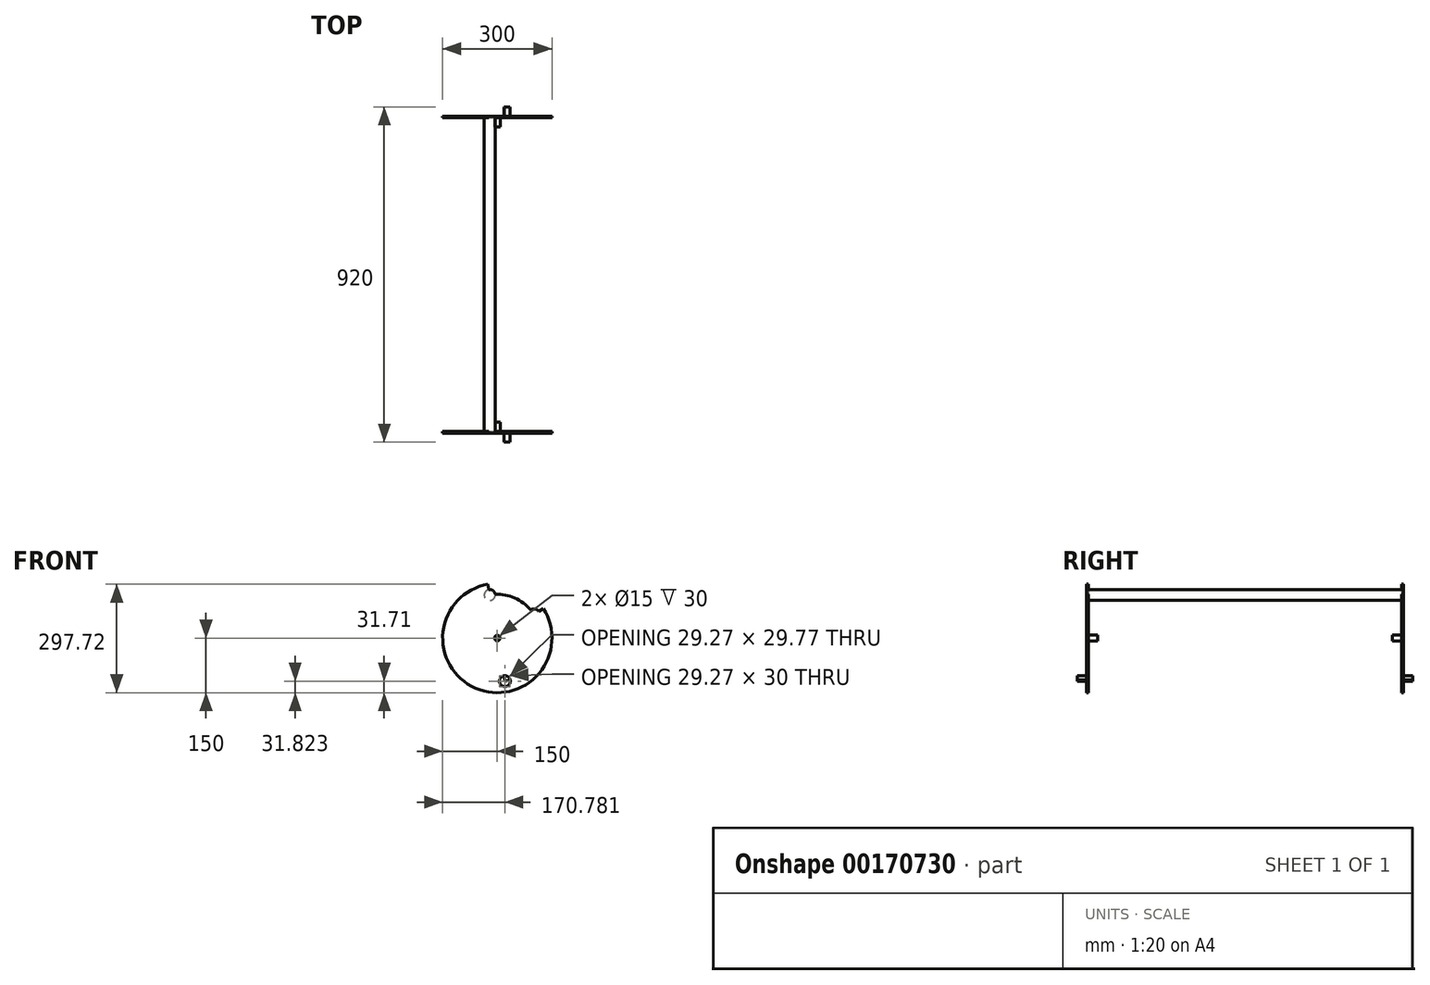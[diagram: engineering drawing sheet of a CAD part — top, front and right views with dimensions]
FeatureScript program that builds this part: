
annotation { "Feature Type Name" : "Feature", "Feature Type Description" : "" }
export const myFeature = defineFeature(function(context is Context, id is Id, definition is map)
    precondition{}
    {
        {
            var Q0;
            Q0=qCreatedBy(makeId("Front.planeOp"),FACE);
            var sketch = newSketch(context, id + "F0", { "sketchPlane" : qUnion([Q0])});
            skCircle(sketch, "E0", {"center": v(0, 0) * mm, "radius": 150 * mm});
            skLineSegment(sketch, "E1", {"start": v(0, 0) * mm, "end": v(459.5, 297.1) * mm});
            skLineSegment(sketch, "E2", {"start": v(0, 0) * mm, "end": v(728.16, 0) * mm});
            skLineSegment(sketch, "E3", {"start": v(0, 0) * mm, "end": v(0, -535.69) * mm});
            skLineSegment(sketch, "E4", {"start": v(125.96, 81.44) * mm, "end": v(100.77, 65.16) * mm});
            skCircle(sketch, "E5", {"center": v(100.77, 65.16) * mm, "radius": 15 * mm});
            skCircle(sketch, "E6", {"center": v(0, 0) * mm, "radius": 8.5 * mm});
            skCircle(sketch, "E7", {"center": v(0, 0) * mm, "radius": 7.5 * mm});
            skLineSegment(sketch, "E8", {"start": v(100.77, 65.16) * mm, "end": v(20.84, -118.18) * mm});
            skLineSegment(sketch, "E9", {"start": v(0, 0) * mm, "end": v(20.84, -118.18) * mm});
            skLineSegment(sketch, "E10", {"start": v(0, 0) * mm, "end": v(34.47, -195.47) * mm});
            skLineSegment(sketch, "E11", {"start": v(34.47, -195.47) * mm, "end": v(-30.52, 173.11) * mm});
            skCircle(sketch, "E12", {"center": v(20.84, -118.18) * mm, "radius": 15 * mm});
            skCircle(sketch, "E13", {"center": v(0, 0) * mm, "radius": 120 * mm});
            skCircle(sketch, "E14", {"center": v(-20.84, 118.18) * mm, "radius": 15 * mm});
            skSolve(sketch);
        }
        {
            var Q0;
            {var subQ0=sQuery(id+"F0.wireOp",EDGE,"E7");var subQ1=sQuery(id+"F0.wireOp",EDGE,"E2");var subQ2=makeQuery(id+"F0.imprint","INTERSECT",VERTEX,{"derivedFrom":[subQ1,subQ0]});Q0=makeQuery(id+"F0.imprint","IMPRINT",FACE,{"disambiguationData":[TD([[makeQuery(id+"F0.imprint","IMPRINT",EDGE,{"disambiguationData":[TD([[subQ2,-1.0]])],"derivedFrom":subQ1}),-1.0]])]});}
            var Q1;
            {var subQ0=sQuery(id+"F0.wireOp",EDGE,"E7");var subQ1=sQuery(id+"F0.wireOp",EDGE,"E1");var subQ2=makeQuery(id+"F0.imprint","INTERSECT",VERTEX,{"derivedFrom":[subQ1,subQ0]});Q1=makeQuery(id+"F0.imprint","IMPRINT",FACE,{"disambiguationData":[TD([[makeQuery(id+"F0.imprint","IMPRINT",EDGE,{"disambiguationData":[TD([[subQ2,-1.0]])],"derivedFrom":subQ1}),-1.0]])]});}
            var Q2;
            {var subQ0=sQuery(id+"F0.wireOp",EDGE,"E7");var subQ1=sQuery(id+"F0.wireOp",EDGE,"E3");var subQ2=makeQuery(id+"F0.imprint","INTERSECT",VERTEX,{"derivedFrom":[subQ1,subQ0]});Q2=makeQuery(id+"F0.imprint","IMPRINT",FACE,{"disambiguationData":[TD([[makeQuery(id+"F0.imprint","IMPRINT",EDGE,{"disambiguationData":[TD([[subQ2,-1.0]])],"derivedFrom":subQ1}),-1.0]])]});}
            var Q3;
            {var subQ0=sQuery(id+"F0.wireOp",EDGE,"E7");var subQ1=sQuery(id+"F0.wireOp",EDGE,"E3");var subQ2=makeQuery(id+"F0.imprint","INTERSECT",VERTEX,{"derivedFrom":[subQ1,subQ0]});Q3=makeQuery(id+"F0.imprint","IMPRINT",FACE,{"disambiguationData":[TD([[makeQuery(id+"F0.imprint","IMPRINT",EDGE,{"disambiguationData":[TD([[subQ2,-1.0]])],"derivedFrom":subQ1}),1.0]])]});}
            var Q4;
            {var subQ0=sQuery(id+"F0.wireOp",EDGE,"E7");var subQ1=sQuery(id+"F0.wireOp",EDGE,"E1");var subQ2=makeQuery(id+"F0.imprint","INTERSECT",VERTEX,{"derivedFrom":[subQ1,subQ0]});Q4=makeQuery(id+"F0.imprint","IMPRINT",FACE,{"disambiguationData":[TD([[makeQuery(id+"F0.imprint","IMPRINT",EDGE,{"disambiguationData":[TD([[subQ2,-1.0]])],"derivedFrom":subQ1}),1.0]])]});}
            extrude(context, id + "F1", {"entities" : qUnion([Q0, Q1, Q2, Q3, Q4]), "oppositeDirection" : true, "depth" : 25 * mm});
        }
        {
            var Q0;
            {var subQ0=sQuery(id+"F0.wireOp",EDGE,"E13");var subQ1=sQuery(id+"F0.wireOp",EDGE,"E11");var subQ2=makeQuery(id+"F0.imprint","INTERSECT",VERTEX,{"derivedFrom":[subQ1,subQ0]});Q0=makeQuery(id+"F0.imprint","IMPRINT",FACE,{"disambiguationData":[TD([[makeQuery(id+"F0.imprint","IMPRINT",EDGE,{"disambiguationData":[TD([[subQ2,-1.0]])],"derivedFrom":subQ1}),-1.0]])]});}
            var Q1;
            {var subQ0=sQuery(id+"F0.wireOp",EDGE,"E13");var subQ1=sQuery(id+"F0.wireOp",EDGE,"E11");var subQ2=makeQuery(id+"F0.imprint","INTERSECT",VERTEX,{"derivedFrom":[subQ1,subQ0]});Q1=makeQuery(id+"F0.imprint","IMPRINT",FACE,{"disambiguationData":[TD([[makeQuery(id+"F0.imprint","IMPRINT",EDGE,{"disambiguationData":[TD([[subQ2,-1.0]])],"derivedFrom":subQ1}),1.0]])]});}
            var Q2;
            {var subQ0=sQuery(id+"F0.wireOp",EDGE,"E14");var subQ1=sQuery(id+"F0.wireOp",EDGE,"E11");var subQ2=makeQuery(id+"F0.imprint","INTERSECT",VERTEX,{"disambiguationData":[OD(0.0)],"derivedFrom":[subQ1,subQ0]});Q2=makeQuery(id+"F0.imprint","IMPRINT",FACE,{"disambiguationData":[TD([[makeQuery(id+"F0.imprint","IMPRINT",EDGE,{"disambiguationData":[TD([[subQ2,-1.0]])],"derivedFrom":subQ1}),1.0]])]});}
            var Q3;
            {var subQ0=sQuery(id+"F0.wireOp",EDGE,"E14");var subQ1=sQuery(id+"F0.wireOp",EDGE,"E11");var subQ2=makeQuery(id+"F0.imprint","INTERSECT",VERTEX,{"disambiguationData":[OD(0.0)],"derivedFrom":[subQ1,subQ0]});Q3=makeQuery(id+"F0.imprint","IMPRINT",FACE,{"disambiguationData":[TD([[makeQuery(id+"F0.imprint","IMPRINT",EDGE,{"disambiguationData":[TD([[subQ2,-1.0]])],"derivedFrom":subQ1}),-1.0]])]});}
            extrude(context, id + "F2", {"entities" : qUnion([Q0, Q1, Q2, Q3]), "operationType" : NewBodyOperationType.ADD, "oppositeDirection" : true, "depth" : (420 + 25) * mm});
        }
        {
            var Q0;
            {var subQ1=sQuery(id+"F0.wireOp",EDGE,"E11");var subQ3=sQuery(id+"F0.wireOp",EDGE,"E12");var subQ4=makeQuery(id+"F0.imprint","INTERSECT",VERTEX,{"disambiguationData":[OD(0.0)],"derivedFrom":[subQ1,subQ3]});Q0=makeQuery(id+"F0.imprint","IMPRINT",FACE,{"disambiguationData":[TD([[makeQuery(id+"F0.imprint","IMPRINT",EDGE,{"disambiguationData":[TD([[subQ4,1.0]])],"derivedFrom":subQ3}),1.0]])]});}
            var Q1;
            {var subQ1=sQuery(id+"F0.wireOp",EDGE,"E11");var subQ3=sQuery(id+"F0.wireOp",EDGE,"E12");var subQ4=makeQuery(id+"F0.imprint","INTERSECT",VERTEX,{"disambiguationData":[OD(0.0)],"derivedFrom":[subQ1,subQ3]});Q1=makeQuery(id+"F0.imprint","IMPRINT",FACE,{"disambiguationData":[TD([[makeQuery(id+"F0.imprint","IMPRINT",EDGE,{"disambiguationData":[TD([[subQ4,-1.0]])],"derivedFrom":subQ3}),1.0]])]});}
            var Q2;
            {var subQ1=sQuery(id+"F0.wireOp",EDGE,"E8");var subQ3=sQuery(id+"F0.wireOp",EDGE,"E12");var subQ4=makeQuery(id+"F0.imprint","INTERSECT",VERTEX,{"derivedFrom":[subQ1,subQ3]});Q2=makeQuery(id+"F0.imprint","IMPRINT",FACE,{"disambiguationData":[TD([[makeQuery(id+"F0.imprint","IMPRINT",EDGE,{"disambiguationData":[TD([[subQ4,1.0]])],"derivedFrom":subQ3}),1.0]])]});}
            var Q3;
            {var subQ1=sQuery(id+"F0.wireOp",EDGE,"E8");var subQ3=sQuery(id+"F0.wireOp",EDGE,"E12");var subQ4=makeQuery(id+"F0.imprint","INTERSECT",VERTEX,{"derivedFrom":[subQ1,subQ3]});Q3=makeQuery(id+"F0.imprint","IMPRINT",FACE,{"disambiguationData":[TD([[makeQuery(id+"F0.imprint","IMPRINT",EDGE,{"disambiguationData":[TD([[subQ4,-1.0]])],"derivedFrom":subQ3}),1.0]])]});}
            var Q4;
            {var subQ1=sQuery(id+"F0.wireOp",EDGE,"E11");var subQ3=sQuery(id+"F0.wireOp",EDGE,"E12");var subQ4=makeQuery(id+"F0.imprint","INTERSECT",VERTEX,{"disambiguationData":[OD(1.0)],"derivedFrom":[subQ1,subQ3]});Q4=makeQuery(id+"F0.imprint","IMPRINT",FACE,{"disambiguationData":[TD([[makeQuery(id+"F0.imprint","IMPRINT",EDGE,{"disambiguationData":[TD([[subQ4,-1.0]])],"derivedFrom":subQ3}),1.0]])]});}
            extrude(context, id + "F3", {"entities" : qUnion([Q0, Q1, Q2, Q3, Q4]), "depth" : 30 * mm});
        }
        {
            var Q0;
            {var subQ5=sQuery(id+"F0.wireOp",EDGE,"E0");var subQ7=sQuery(id+"F0.wireOp",EDGE,"E2");var subQ8=makeQuery(id+"F0.imprint","INTERSECT",VERTEX,{"derivedFrom":[subQ5,subQ7]});Q0=makeQuery(id+"F0.imprint","IMPRINT",FACE,{"disambiguationData":[TD([[makeQuery(id+"F0.imprint","IMPRINT",EDGE,{"disambiguationData":[TD([[subQ8,1.0]])],"derivedFrom":subQ5}),1.0]])]});}
            var Q1;
            {var subQ0=sQuery(id+"F0.wireOp",EDGE,"E8");var subQ1=sQuery(id+"F0.wireOp",EDGE,"E2");var subQ2=makeQuery(id+"F0.imprint","INTERSECT",VERTEX,{"derivedFrom":[subQ1,subQ0]});Q1=makeQuery(id+"F0.imprint","IMPRINT",FACE,{"disambiguationData":[TD([[makeQuery(id+"F0.imprint","IMPRINT",EDGE,{"disambiguationData":[TD([[subQ2,-1.0]])],"derivedFrom":subQ1}),-1.0]])]});}
            var Q2;
            {var subQ1=sQuery(id+"F0.wireOp",EDGE,"E4");var subQ6=sQuery(id+"F0.wireOp",EDGE,"E0");var subQ9=makeQuery(id+"F0.imprint","INTERSECT",VERTEX,{"derivedFrom":[subQ6,subQ1]});Q2=makeQuery(id+"F0.imprint","IMPRINT",FACE,{"disambiguationData":[TD([[makeQuery(id+"F0.imprint","IMPRINT",EDGE,{"disambiguationData":[TD([[subQ9,1.0]])],"derivedFrom":subQ6}),1.0]])]});}
            var Q3;
            {var subQ0=sQuery(id+"F0.wireOp",EDGE,"E8");var subQ1=sQuery(id+"F0.wireOp",EDGE,"E2");var subQ2=makeQuery(id+"F0.imprint","INTERSECT",VERTEX,{"derivedFrom":[subQ1,subQ0]});Q3=makeQuery(id+"F0.imprint","IMPRINT",FACE,{"disambiguationData":[TD([[makeQuery(id+"F0.imprint","IMPRINT",EDGE,{"disambiguationData":[TD([[subQ2,-1.0]])],"derivedFrom":subQ1}),1.0]])]});}
            var Q4;
            {var subQ0=sQuery(id+"F0.wireOp",EDGE,"E8");var subQ1=sQuery(id+"F0.wireOp",EDGE,"E5");var subQ2=makeQuery(id+"F0.imprint","INTERSECT",VERTEX,{"derivedFrom":[subQ1,subQ0]});Q4=makeQuery(id+"F0.imprint","IMPRINT",FACE,{"disambiguationData":[TD([[makeQuery(id+"F0.imprint","IMPRINT",EDGE,{"disambiguationData":[TD([[subQ2,-1.0]])],"derivedFrom":subQ1}),1.0]])]});}
            var Q5;
            {var subQ1=sQuery(id+"F0.wireOp",EDGE,"E4");var subQ3=sQuery(id+"F0.wireOp",EDGE,"E5");var subQ4=makeQuery(id+"F0.imprint","INTERSECT",VERTEX,{"derivedFrom":[subQ1,subQ3]});Q5=makeQuery(id+"F0.imprint","IMPRINT",FACE,{"disambiguationData":[TD([[makeQuery(id+"F0.imprint","IMPRINT",EDGE,{"disambiguationData":[TD([[subQ4,1.0]])],"derivedFrom":subQ3}),1.0]])]});}
            var Q6;
            {var subQ1=sQuery(id+"F0.wireOp",EDGE,"E4");var subQ3=sQuery(id+"F0.wireOp",EDGE,"E5");var subQ4=makeQuery(id+"F0.imprint","INTERSECT",VERTEX,{"derivedFrom":[subQ1,subQ3]});Q6=makeQuery(id+"F0.imprint","IMPRINT",FACE,{"disambiguationData":[TD([[makeQuery(id+"F0.imprint","IMPRINT",EDGE,{"disambiguationData":[TD([[subQ4,-1.0]])],"derivedFrom":subQ3}),1.0]])]});}
            var Q7;
            {var subQ1=sQuery(id+"F0.wireOp",EDGE,"E1");var subQ3=sQuery(id+"F0.wireOp",EDGE,"E5");var subQ4=makeQuery(id+"F0.imprint","INTERSECT",VERTEX,{"derivedFrom":[subQ1,subQ3]});Q7=makeQuery(id+"F0.imprint","IMPRINT",FACE,{"disambiguationData":[TD([[makeQuery(id+"F0.imprint","IMPRINT",EDGE,{"disambiguationData":[TD([[subQ4,1.0]])],"derivedFrom":subQ3}),1.0]])]});}
            var Q8;
            {var subQ1=sQuery(id+"F0.wireOp",EDGE,"E0");var subQ6=sQuery(id+"F0.wireOp",EDGE,"E4");var subQ10=makeQuery(id+"F0.imprint","INTERSECT",VERTEX,{"derivedFrom":[subQ1,subQ6]});Q8=makeQuery(id+"F0.imprint","IMPRINT",FACE,{"disambiguationData":[TD([[makeQuery(id+"F0.imprint","IMPRINT",EDGE,{"disambiguationData":[TD([[subQ10,-1.0]])],"derivedFrom":subQ1}),1.0]])]});}
            var Q9;
            {var subQ1=sQuery(id+"F0.wireOp",EDGE,"E6");var subQ5=sQuery(id+"F0.wireOp",EDGE,"E1");var subQ6=makeQuery(id+"F0.imprint","INTERSECT",VERTEX,{"derivedFrom":[subQ5,subQ1]});Q9=makeQuery(id+"F0.imprint","IMPRINT",FACE,{"disambiguationData":[TD([[makeQuery(id+"F0.imprint","IMPRINT",EDGE,{"disambiguationData":[TD([[subQ6,-1.0]])],"derivedFrom":subQ5}),1.0]])]});}
            var Q10;
            {var subQ0=sQuery(id+"F0.wireOp",EDGE,"E6");var subQ1=sQuery(id+"F0.wireOp",EDGE,"E1");var subQ2=makeQuery(id+"F0.imprint","INTERSECT",VERTEX,{"derivedFrom":[subQ1,subQ0]});Q10=makeQuery(id+"F0.imprint","IMPRINT",FACE,{"disambiguationData":[TD([[makeQuery(id+"F0.imprint","IMPRINT",EDGE,{"disambiguationData":[TD([[subQ2,-1.0]])],"derivedFrom":subQ1}),-1.0]])]});}
            var Q11;
            {var subQ1=sQuery(id+"F0.wireOp",EDGE,"E2");var subQ6=sQuery(id+"F0.wireOp",EDGE,"E6");var subQ9=makeQuery(id+"F0.imprint","INTERSECT",VERTEX,{"derivedFrom":[subQ1,subQ6]});Q11=makeQuery(id+"F0.imprint","IMPRINT",FACE,{"disambiguationData":[TD([[makeQuery(id+"F0.imprint","IMPRINT",EDGE,{"disambiguationData":[TD([[subQ9,-1.0]])],"derivedFrom":subQ1}),-1.0]])]});}
            var Q12;
            {var subQ1=sQuery(id+"F0.wireOp",EDGE,"E3");var subQ7=sQuery(id+"F0.wireOp",EDGE,"E6");var subQ9=makeQuery(id+"F0.imprint","INTERSECT",VERTEX,{"derivedFrom":[subQ1,subQ7]});Q12=makeQuery(id+"F0.imprint","IMPRINT",FACE,{"disambiguationData":[TD([[makeQuery(id+"F0.imprint","IMPRINT",EDGE,{"disambiguationData":[TD([[subQ9,-1.0]])],"derivedFrom":subQ1}),-1.0]])]});}
            var Q13;
            {var subQ5=sQuery(id+"F0.wireOp",EDGE,"E0");var subQ7=sQuery(id+"F0.wireOp",EDGE,"E11");var subQ8=makeQuery(id+"F0.imprint","INTERSECT",VERTEX,{"disambiguationData":[OD(0.0)],"derivedFrom":[subQ5,subQ7]});Q13=makeQuery(id+"F0.imprint","IMPRINT",FACE,{"disambiguationData":[TD([[makeQuery(id+"F0.imprint","IMPRINT",EDGE,{"disambiguationData":[TD([[subQ8,-1.0]])],"derivedFrom":subQ5}),1.0]])]});}
            var Q14;
            {var subQ1=sQuery(id+"F0.wireOp",EDGE,"E6");var subQ5=sQuery(id+"F0.wireOp",EDGE,"E3");var subQ6=makeQuery(id+"F0.imprint","INTERSECT",VERTEX,{"derivedFrom":[subQ5,subQ1]});Q14=makeQuery(id+"F0.imprint","IMPRINT",FACE,{"disambiguationData":[TD([[makeQuery(id+"F0.imprint","IMPRINT",EDGE,{"disambiguationData":[TD([[subQ6,-1.0]])],"derivedFrom":subQ5}),1.0]])]});}
            var Q15;
            {var subQ5=sQuery(id+"F0.wireOp",EDGE,"E0");var subQ7=sQuery(id+"F0.wireOp",EDGE,"E3");var subQ9=makeQuery(id+"F0.imprint","INTERSECT",VERTEX,{"derivedFrom":[subQ5,subQ7]});Q15=makeQuery(id+"F0.imprint","IMPRINT",FACE,{"disambiguationData":[TD([[makeQuery(id+"F0.imprint","IMPRINT",EDGE,{"disambiguationData":[TD([[subQ9,-1.0]])],"derivedFrom":subQ5}),1.0]])]});}
            var Q16;
            {var subQ0=sQuery(id+"F0.wireOp",EDGE,"E13");var subQ1=sQuery(id+"F0.wireOp",EDGE,"E11");var subQ2=makeQuery(id+"F0.imprint","INTERSECT",VERTEX,{"derivedFrom":[subQ1,subQ0]});Q16=makeQuery(id+"F0.imprint","IMPRINT",FACE,{"disambiguationData":[TD([[makeQuery(id+"F0.imprint","IMPRINT",EDGE,{"disambiguationData":[TD([[subQ2,-1.0]])],"derivedFrom":subQ1}),1.0]])]});}
            var Q17;
            {var subQ0=sQuery(id+"F0.wireOp",EDGE,"E14");var subQ1=sQuery(id+"F0.wireOp",EDGE,"E11");var subQ2=makeQuery(id+"F0.imprint","INTERSECT",VERTEX,{"disambiguationData":[OD(0.0)],"derivedFrom":[subQ1,subQ0]});Q17=makeQuery(id+"F0.imprint","IMPRINT",FACE,{"disambiguationData":[TD([[makeQuery(id+"F0.imprint","IMPRINT",EDGE,{"disambiguationData":[TD([[subQ2,-1.0]])],"derivedFrom":subQ1}),1.0]])]});}
            var Q18;
            {var subQ0=sQuery(id+"F0.wireOp",EDGE,"E14");var subQ1=sQuery(id+"F0.wireOp",EDGE,"E11");var subQ2=makeQuery(id+"F0.imprint","INTERSECT",VERTEX,{"disambiguationData":[OD(0.0)],"derivedFrom":[subQ1,subQ0]});Q18=makeQuery(id+"F0.imprint","IMPRINT",FACE,{"disambiguationData":[TD([[makeQuery(id+"F0.imprint","IMPRINT",EDGE,{"disambiguationData":[TD([[subQ2,-1.0]])],"derivedFrom":subQ1}),-1.0]])]});}
            var Q19;
            {var subQ0=sQuery(id+"F0.wireOp",EDGE,"E13");var subQ1=sQuery(id+"F0.wireOp",EDGE,"E11");var subQ2=makeQuery(id+"F0.imprint","INTERSECT",VERTEX,{"derivedFrom":[subQ1,subQ0]});Q19=makeQuery(id+"F0.imprint","IMPRINT",FACE,{"disambiguationData":[TD([[makeQuery(id+"F0.imprint","IMPRINT",EDGE,{"disambiguationData":[TD([[subQ2,-1.0]])],"derivedFrom":subQ1}),-1.0]])]});}
            var Q20;
            {var subQ1=sQuery(id+"F0.wireOp",EDGE,"E1");var subQ3=sQuery(id+"F0.wireOp",EDGE,"E5");var subQ4=makeQuery(id+"F0.imprint","INTERSECT",VERTEX,{"derivedFrom":[subQ1,subQ3]});Q20=makeQuery(id+"F0.imprint","IMPRINT",FACE,{"disambiguationData":[TD([[makeQuery(id+"F0.imprint","IMPRINT",EDGE,{"disambiguationData":[TD([[subQ4,-1.0]])],"derivedFrom":subQ3}),1.0]])]});}
            var Q21;
            {var subQ0=sQuery(id+"F0.wireOp",EDGE,"E7");var subQ1=sQuery(id+"F0.wireOp",EDGE,"E2");var subQ2=makeQuery(id+"F0.imprint","INTERSECT",VERTEX,{"derivedFrom":[subQ1,subQ0]});Q21=makeQuery(id+"F0.imprint","IMPRINT",FACE,{"disambiguationData":[TD([[makeQuery(id+"F0.imprint","IMPRINT",EDGE,{"disambiguationData":[TD([[subQ2,-1.0]])],"derivedFrom":subQ1}),-1.0]])]});}
            var Q22;
            {var subQ0=sQuery(id+"F0.wireOp",EDGE,"E7");var subQ1=sQuery(id+"F0.wireOp",EDGE,"E3");var subQ2=makeQuery(id+"F0.imprint","INTERSECT",VERTEX,{"derivedFrom":[subQ1,subQ0]});Q22=makeQuery(id+"F0.imprint","IMPRINT",FACE,{"disambiguationData":[TD([[makeQuery(id+"F0.imprint","IMPRINT",EDGE,{"disambiguationData":[TD([[subQ2,-1.0]])],"derivedFrom":subQ1}),1.0]])]});}
            var Q23;
            {var subQ0=sQuery(id+"F0.wireOp",EDGE,"E7");var subQ1=sQuery(id+"F0.wireOp",EDGE,"E3");var subQ2=makeQuery(id+"F0.imprint","INTERSECT",VERTEX,{"derivedFrom":[subQ1,subQ0]});Q23=makeQuery(id+"F0.imprint","IMPRINT",FACE,{"disambiguationData":[TD([[makeQuery(id+"F0.imprint","IMPRINT",EDGE,{"disambiguationData":[TD([[subQ2,-1.0]])],"derivedFrom":subQ1}),-1.0]])]});}
            var Q24;
            {var subQ0=sQuery(id+"F0.wireOp",EDGE,"E7");var subQ1=sQuery(id+"F0.wireOp",EDGE,"E1");var subQ2=makeQuery(id+"F0.imprint","INTERSECT",VERTEX,{"derivedFrom":[subQ1,subQ0]});Q24=makeQuery(id+"F0.imprint","IMPRINT",FACE,{"disambiguationData":[TD([[makeQuery(id+"F0.imprint","IMPRINT",EDGE,{"disambiguationData":[TD([[subQ2,-1.0]])],"derivedFrom":subQ1}),-1.0]])]});}
            var Q25;
            {var subQ0=sQuery(id+"F0.wireOp",EDGE,"E7");var subQ1=sQuery(id+"F0.wireOp",EDGE,"E1");var subQ2=makeQuery(id+"F0.imprint","INTERSECT",VERTEX,{"derivedFrom":[subQ1,subQ0]});Q25=makeQuery(id+"F0.imprint","IMPRINT",FACE,{"disambiguationData":[TD([[makeQuery(id+"F0.imprint","IMPRINT",EDGE,{"disambiguationData":[TD([[subQ2,-1.0]])],"derivedFrom":subQ1}),1.0]])]});}
            var Q26;
            Q26=sQuery(id+"F0.wireOp",EDGE,"E0");
            extrude(context, id + "F4", {"entities" : qUnion([Q0, Q1, Q2, Q3, Q4, Q5, Q6, Q7, Q8, Q9, Q10, Q11, Q12, Q13, Q14, Q15, Q16, Q17, Q18, Q19, Q20, Q21, Q22, Q23, Q24, Q25]), "operationType" : NewBodyOperationType.ADD, "surfaceEntities" : qUnion([Q26]), "depth" : 5 * mm});
        }
        {
            var Q0;
            Q0=qCreatedBy(makeId("Front.planeOp"),FACE);
            cPlane(context, id + "F5", {"entities" : qUnion([Q0]), "cplaneType" : CPlaneType.OFFSET, "offset" : (420 + 10) * mm, "oppositeDirection" : true, "width" : 150 * mm, "height" : 150 * mm});
        }
        {
            var Q0;
            Q0=makeQuery(id+"F1.opExtrude","SWEPT_BODY",BODY,{"disambiguationData":[OSD([sQuery(id+"F0.wireOp",EDGE,"E6"),sQuery(id+"F0.wireOp",EDGE,"E7")])]});
            var Q1;
            Q1=makeQuery(id+"F3.opExtrude","SWEPT_BODY",BODY,{"disambiguationData":[OSD([sQuery(id+"F0.wireOp",EDGE,"E12")])]});
            var Q2;
            Q2=makeQuery(id+"F4.opExtrude","SWEPT_BODY",BODY,{"disambiguationData":[OSD([sQuery(id+"F0.wireOp",EDGE,"E0"),sQuery(id+"F0.wireOp",EDGE,"E6"),sQuery(id+"F0.wireOp",EDGE,"E12")])]});
            var Q3;
            Q3=makeQuery(id+"F2.opExtrude","SWEPT_BODY",BODY,{"disambiguationData":[OSD([sQuery(id+"F0.wireOp",EDGE,"E14")])]});
            var Q4;
            Q4=qCreatedBy(id+"F5.planeOp",FACE);
            mirror(context, id + "F6", {"operationType" : NewBodyOperationType.ADD, "entities" : qUnion([Q0, Q1, Q2, Q3]), "mirrorPlane" : qUnion([Q4])});
        }
    });
